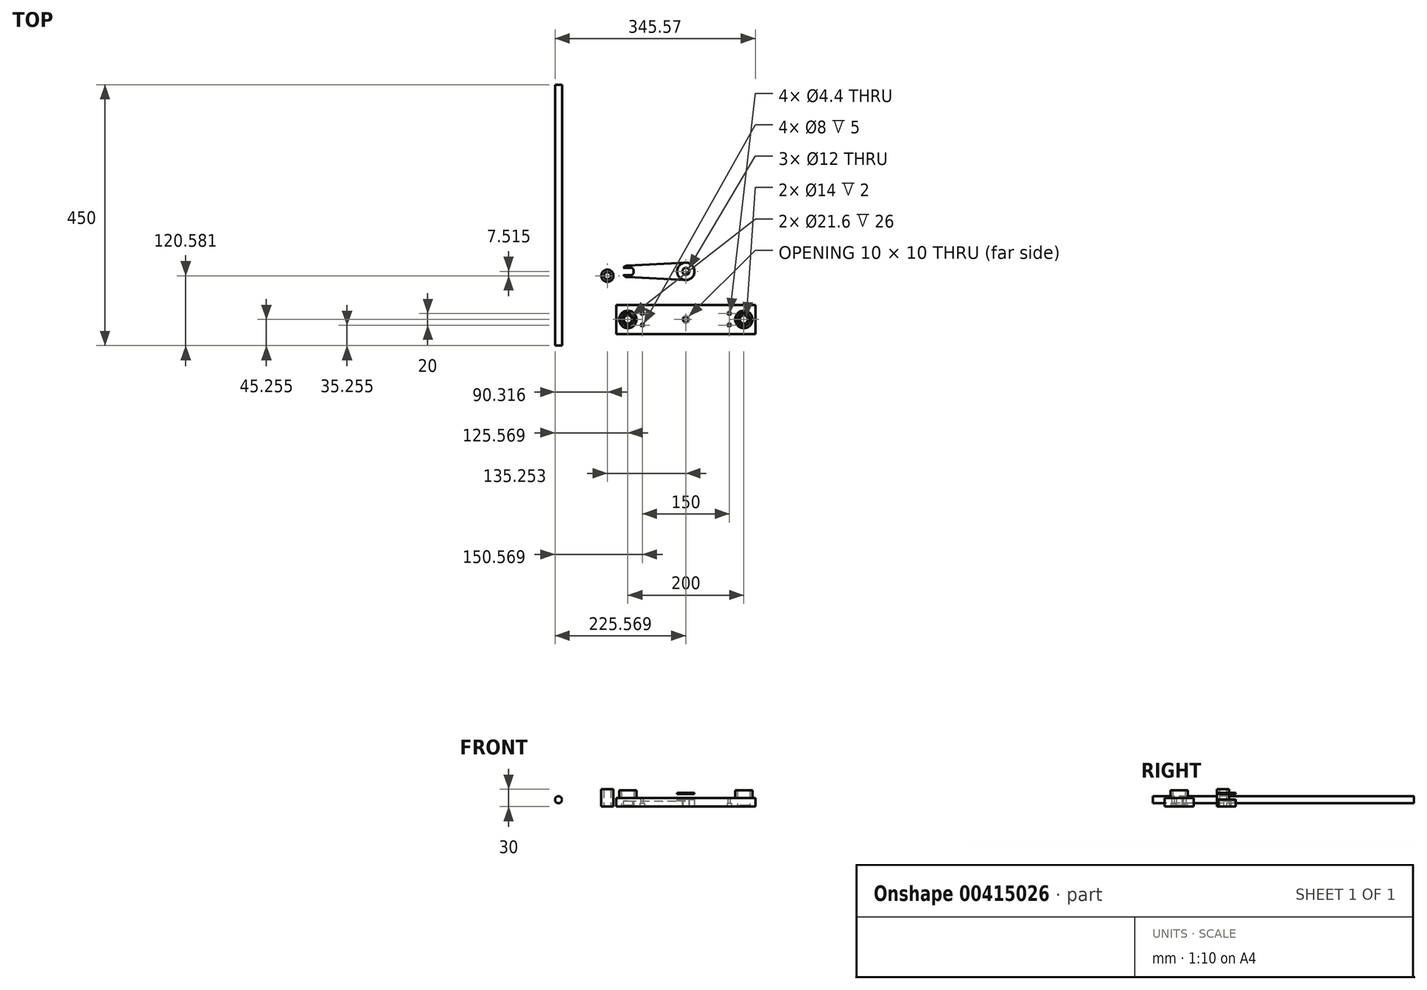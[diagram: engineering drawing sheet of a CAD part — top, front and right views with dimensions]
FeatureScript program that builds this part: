
annotation { "Feature Type Name" : "Feature", "Feature Type Description" : "" }
export const myFeature = defineFeature(function(context is Context, id is Id, definition is map)
    precondition{}
    {
        {
            var Q0;
            Q0=qCreatedBy(makeId("Front.planeOp"),FACE);
            var sketch = newSketch(context, id + "F0", { "sketchPlane" : qUnion([Q0])});
            skCircle(sketch, "E0", {"center": v(-58.63, 11.82) * mm, "radius": 6 * mm});
            skSolve(sketch);
        }
        {
            var Q0;
            Q0 = qSketchRegion(id + "F0", true);
            extrude(context, id + "F1", {"entities" : qUnion([Q0]), "oppositeDirection" : true, "depth" : 450 * mm});
        }
        {
            var Q0;
            Q0=qCreatedBy(makeId("Top.planeOp"),FACE);
            var sketch = newSketch(context, id + "F2", { "sketchPlane" : qUnion([Q0])});
            skLineSegment(sketch, "E1.bottom", {"start": v(40.94, 70.25) * mm, "end": v(280.94, 70.25) * mm});
            skLineSegment(sketch, "E1.top", {"start": v(40.94, 20.25) * mm, "end": v(280.94, 20.25) * mm});
            skLineSegment(sketch, "E1.left", {"start": v(40.94, 70.25) * mm, "end": v(40.94, 20.25) * mm});
            skLineSegment(sketch, "E1.right", {"start": v(280.94, 70.25) * mm, "end": v(280.94, 20.25) * mm});
            skCircle(sketch, "E2", {"center": v(60.94, 45.25) * mm, "radius": 7 * mm});
            skCircle(sketch, "E3", {"center": v(160.94, 45.25) * mm, "radius": 5 * mm});
            skCircle(sketch, "E4", {"center": v(260.94, 45.25) * mm, "radius": 7 * mm});
            skLineSegment(sketch, "E5", {"start": v(40.94, 40.02) * mm, "end": v(160.94, 40.25) * mm});
            skLineSegment(sketch, "E6", {"start": v(160.94, 40.25) * mm, "end": v(280.94, 40.48) * mm});
            skLineSegment(sketch, "E7", {"start": v(112.62, 70.25) * mm, "end": v(112.67, 45.25) * mm});
            skLineSegment(sketch, "E8", {"start": v(112.67, 45.25) * mm, "end": v(112.71, 20.25) * mm});
            skSolve(sketch);
        }
        {
            var Q0;
            Q0 = qSketchRegion(id + "F2", true);
            extrude(context, id + "F3", {"entities" : qUnion([Q0]), "depth" : 15 * mm});
        }
        {
            var Q0;
            Q0=qCreatedBy(makeId("Top.planeOp"),FACE);
            cPlane(context, id + "F4", {"entities" : qUnion([Q0]), "cplaneType" : CPlaneType.OFFSET, "offset" : 2 * mm, "width" : 150 * mm, "height" : 150 * mm});
        }
        {
            var Q0;
            Q0=qCreatedBy(id+"F4.planeOp",FACE);
            var sketch = newSketch(context, id + "F5", { "sketchPlane" : qUnion([Q0])});
            skCircle(sketch, "E9", {"center": v(60.94, 45.25) * mm, "radius": 10.8 * mm});
            skCircle(sketch, "E10", {"center": v(260.94, 45.25) * mm, "radius": 10.8 * mm});
            skCircle(sketch, "E11", {"center": v(60.94, 45.25) * mm, "radius": 15 * mm});
            skCircle(sketch, "E12", {"center": v(260.94, 45.25) * mm, "radius": 15 * mm});
            skSolve(sketch);
        }
        {
            var Q0;
            Q0 = qSketchRegion(id + "F5", true);
            extrude(context, id + "F6", {"entities" : qUnion([Q0]), "operationType" : NewBodyOperationType.ADD, "depth" : 26 * mm});
        }
        {
            var Q0;
            Q0=makeQuery(id+"F5.imprint","IMPRINT",FACE,{"disambiguationData":[TD([[makeQuery(id+"F5.imprint","IMPRINT",EDGE,{"derivedFrom":sQuery(id+"F5.wireOp",EDGE,"E10")}),1.0]])]});
            var Q1;
            Q1=makeQuery(id+"F5.imprint","IMPRINT",FACE,{"disambiguationData":[TD([[makeQuery(id+"F5.imprint","IMPRINT",EDGE,{"derivedFrom":sQuery(id+"F5.wireOp",EDGE,"E9")}),1.0]])]});
            extrude(context, id + "F7", {"entities" : qUnion([Q0, Q1]), "operationType" : NewBodyOperationType.REMOVE, "depth" : 25 * mm});
        }
        {
            var Q0;
            Q0=qCreatedBy(makeId("Top.planeOp"),FACE);
            var sketch = newSketch(context, id + "F8", { "sketchPlane" : qUnion([Q0])});
            skCircle(sketch, "E13", {"center": v(25.69, 120.58) * mm, "radius": 6 * mm});
            skCircle(sketch, "E14", {"center": v(25.69, 120.58) * mm, "radius": 10.5 * mm});
            skSolve(sketch);
        }
        {
            var Q0;
            Q0 = qSketchRegion(id + "F8", true);
            extrude(context, id + "F9", {"entities" : qUnion([Q0]), "depth" : 30 * mm});
        }
        {
            var Q0;
            Q0=qCreatedBy(makeId("Top.planeOp"),FACE);
            var sketch = newSketch(context, id + "F10", { "sketchPlane" : qUnion([Q0])});
            skCircle(sketch, "E15", {"center": v(160.94, 128.1) * mm, "radius": 15 * mm});
            skCircle(sketch, "E16", {"center": v(160.94, 128.1) * mm, "radius": 6 * mm});
            skArc(sketch, "E17", {"start": v(53.13, 121.85) * mm, "mid": v(70.94, 128.1) * mm, "end": v(53.13, 134.35) * mm});
            skLineSegment(sketch, "E18", {"start": v(60.44, 138.08) * mm, "end": v(160.19, 143.08) * mm});
            skLineSegment(sketch, "E19", {"start": v(60.44, 118.1) * mm, "end": v(160.19, 113.12) * mm});
            skLineSegment(sketch, "E20.bottom", {"start": v(53.13, 134.35) * mm, "end": v(75.5, 134.35) * mm});
            skLineSegment(sketch, "E20.top", {"start": v(53.13, 121.85) * mm, "end": v(75.5, 121.85) * mm});
            skLineSegment(sketch, "E20.right", {"start": v(75.5, 134.35) * mm, "end": v(75.5, 121.85) * mm});
            skSolve(sketch);
        }
        {
            var Q0;
            Q0 = qSketchRegion(id + "F10", true);
            extrude(context, id + "F11", {"entities" : qUnion([Q0]), "depth" : 10 * mm});
        }
        {
            var Q0;
            Q0=makeQuery(id+"F10.imprint","IMPRINT",FACE,{"disambiguationData":[TD([[makeQuery(id+"F10.imprint","IMPRINT",EDGE,{"derivedFrom":sQuery(id+"F10.wireOp",EDGE,"E16")}),-1.0]])]});
            extrude(context, id + "F12", {"entities" : qUnion([Q0]), "operationType" : NewBodyOperationType.ADD, "depth" : 12 * mm});
        }
        {
            var Q0;
            Q0=makeQuery(id+"F12.opExtrude","CAP_FACE",FACE,{"disambiguationData":[OSD([sQuery(id+"F10.wireOp",EDGE,"E15"),sQuery(id+"F10.wireOp",EDGE,"E16")])],"isStart":false});
            cPlane(context, id + "F13", {"entities" : qUnion([Q0]), "cplaneType" : CPlaneType.OFFSET, "offset" : 10 * mm, "width" : 150 * mm, "height" : 150 * mm});
        }
        {
            var Q0;
            Q0=qCreatedBy(id+"F13.planeOp",FACE);
            var sketch = newSketch(context, id + "F14", { "sketchPlane" : qUnion([Q0])});
            skCircle(sketch, "E21", {"center": v(160.94, 128.1) * mm, "radius": 15 * mm});
            skCircle(sketch, "E22", {"center": v(160.94, 128.1) * mm, "radius": 6 * mm});
            skSolve(sketch);
        }
        {
            var Q0;
            Q0 = qSketchRegion(id + "F14", true);
            extrude(context, id + "F15", {"entities" : qUnion([Q0]), "depth" : 2 * mm});
        }
        {
            var Q0;
            {var subQ0=sQuery(id+"F2.wireOp",EDGE,"E1.left");var subQ1=sQuery(id+"F2.wireOp",EDGE,"E1.top");var subQ2=sQuery(id+"F2.wireOp",EDGE,"E1.right");var subQ3=sQuery(id+"F2.wireOp",EDGE,"E1.bottom");var subQ4=sQuery(id+"F2.wireOp",EDGE,"E3");Q0=makeQuery(id+"F6.boolean.opBoolean","SPLIT",FACE,{"disambiguationData":[TD([makeQuery(id+"F3.opExtrude","SWEPT_FACE",FACE,{"disambiguationData":[OSD([subQ3])]})])],"derivedFrom":makeQuery(id+"F3.opExtrude","CAP_FACE",FACE,{"disambiguationData":[OSD([subQ3,subQ1,subQ0,subQ2,sQuery(id+"F2.wireOp",EDGE,"E2"),subQ4,sQuery(id+"F2.wireOp",EDGE,"E4")])],"isStart":false})});}
            var sketch = newSketch(context, id + "F16", { "sketchPlane" : qUnion([Q0])});
            skCircle(sketch, "E23", {"center": v(85.94, 55.25) * mm, "radius": 2.2 * mm});
            skCircle(sketch, "E24", {"center": v(85.94, 35.25) * mm, "radius": 2.2 * mm});
            skLineSegment(sketch, "E25", {"start": v(160.94, 45.25) * mm, "end": v(160.94, 70.25) * mm});
            skCircle(sketch, "E26.MirrorC", {"center": v(235.94, 55.25) * mm, "radius": 2.2 * mm});
            skCircle(sketch, "E27.MirrorC", {"center": v(235.94, 35.25) * mm, "radius": 2.2 * mm});
            skSolve(sketch);
        }
        {
            var Q0;
            Q0 = qSketchRegion(id + "F16", true);
            extrude(context, id + "F17", {"entities" : qUnion([Q0]), "operationType" : NewBodyOperationType.REMOVE, "oppositeDirection" : true, "depth" : 25 * mm});
        }
        {
            var Q0;
            {var subQ9=sQuery(id+"F2.wireOp",EDGE,"E1.top");var subQ12=sQuery(id+"F2.wireOp",EDGE,"E1.right");var subQ13=makeQuery(id+"F2.imprint","INTERSECT",VERTEX,{"derivedFrom":[subQ9,subQ12]});Q0=makeQuery(id+"F2.imprint","IMPRINT",FACE,{"disambiguationData":[TD([[makeQuery(id+"F2.imprint","IMPRINT",EDGE,{"disambiguationData":[TD([[subQ13,1.0]])],"derivedFrom":subQ9}),1.0]])]});}
            var sketch = newSketch(context, id + "F18", { "sketchPlane" : qUnion([Q0])});
            skCircle(sketch, "E28", {"center": v(85.94, 35.25) * mm, "radius": 4 * mm});
            skCircle(sketch, "E29", {"center": v(85.94, 55.25) * mm, "radius": 4 * mm});
            skLineSegment(sketch, "E30", {"start": v(160.94, 60.17) * mm, "end": v(160.94, 26.73) * mm});
            skCircle(sketch, "E31.MirrorC", {"center": v(235.94, 35.25) * mm, "radius": 4 * mm});
            skCircle(sketch, "E32.MirrorC", {"center": v(235.94, 55.25) * mm, "radius": 4 * mm});
            skSolve(sketch);
        }
        {
            var Q0;
            Q0 = qSketchRegion(id + "F18", true);
            extrude(context, id + "F19", {"entities" : qUnion([Q0]), "operationType" : NewBodyOperationType.REMOVE, "depth" : 5 * mm});
        }
    });
